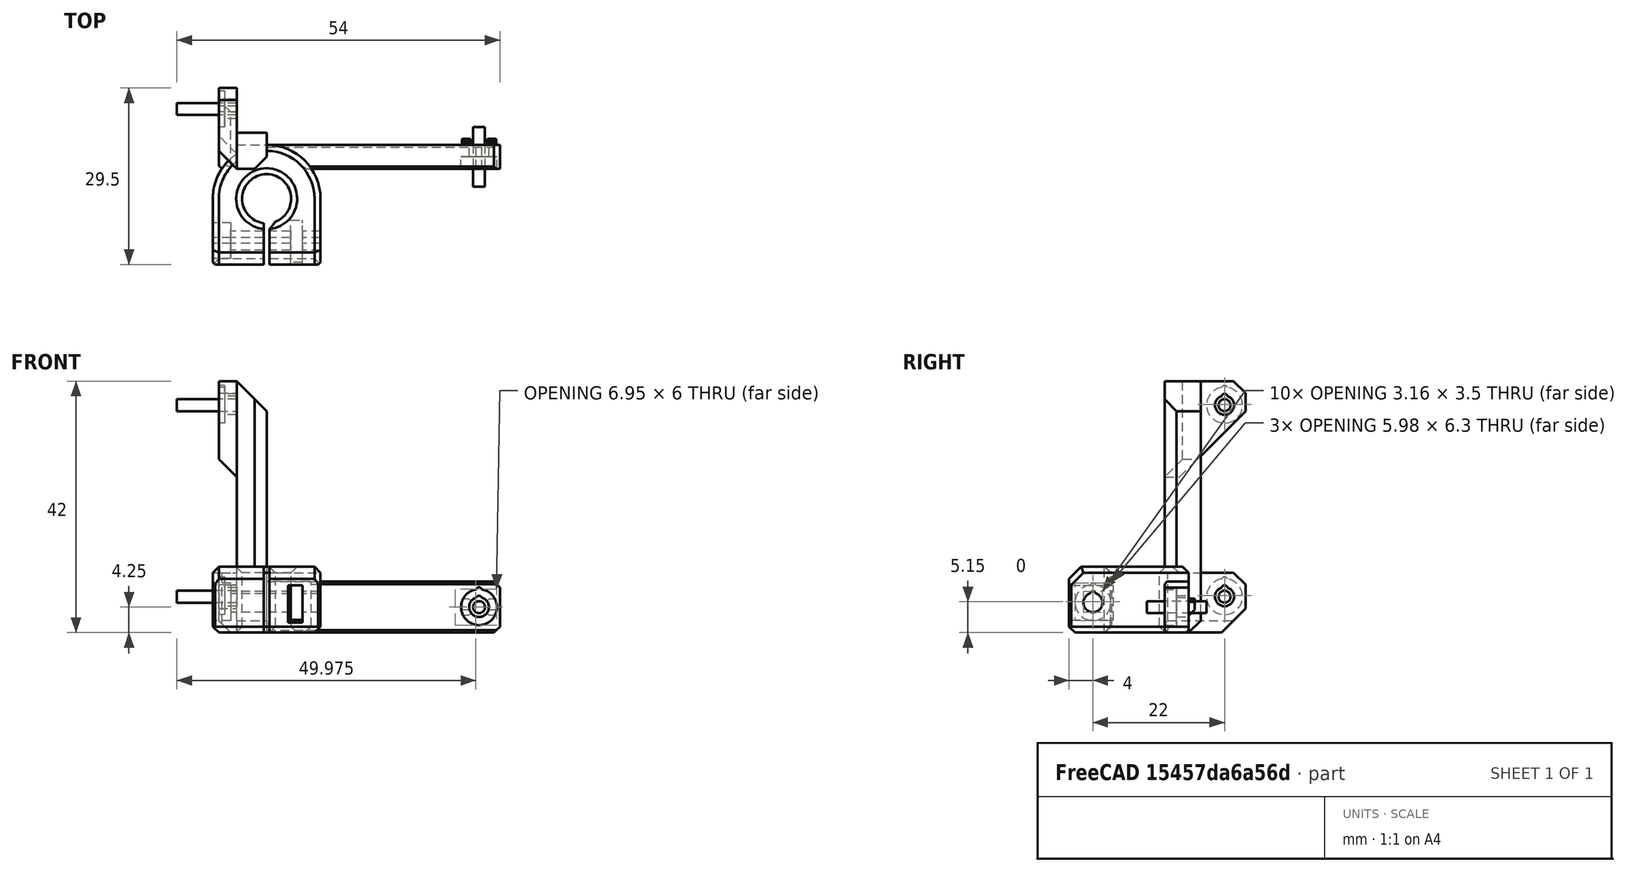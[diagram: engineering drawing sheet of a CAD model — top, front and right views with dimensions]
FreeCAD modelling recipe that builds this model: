
FCSTD DOCUMENT  (FreeCAD 0.18R14555 (Git shallow))
Label: bear-mera-probe-mount
License: All rights reserved
LicenseURL: http://en.wikipedia.org/wiki/All_rights_reserved
objects: Part::Chamfer×19, Part::Cylinder×15, Part::Box×11, Part::Cut×10, Part::MultiFuse×8, Part::Feature×3
note: 66 computed .brp shape members not serialized (recipe doc carries the construction recipe); baked Part::Feature solids carry a one-line shape summary decoded from their .brp

FEATURE [Part::Box] Box001  label="Cube001"
  AttacherType = Attacher::AttachEngine3D
  Height = 8.5
  Length = 44
  Width = 4
FEATURE [Part::Box] Box002  label="Cube002"
  AttacherType = Attacher::AttachEngine3D
  Height = 42
  Length = 5
  Width = 6
FEATURE [Part::Box] Box  label="Cube"
  AttacherType = Attacher::AttachEngine3D
  Height = 10
  Length = 3
  Placement = pos=(-3,0,0) rot=(0,0,1;0rad)
  Width = 13.5
FEATURE [Part::Box] Box003  label="Cube003"
  AttacherType = Attacher::AttachEngine3D
  Height = 16
  Length = 3
  Placement = pos=(-3,0,26) rot=(0,0,1;0rad)
  Width = 13.5
FEATURE [Part::Cylinder] Cylinder
  Angle = 360
  AttacherType = Attacher::AttachEngine3D
  Height = 1
  Placement = pos=(-2,9.5,8.8) rot=(0,-1,0;1.5708rad)
  Radius = 0.5
FEATURE [Part::Cylinder] Cylinder001
  Angle = 360
  AttacherType = Attacher::AttachEngine3D
  Height = 1
  Placement = pos=(-2,9.5,40.8) rot=(0,-1,0;1.5708rad)
  Radius = 0.5
FEATURE [Part::Box] Box004  label="Cube004"
  AttacherType = Attacher::AttachEngine3D
  Height = 10
  Length = 10
  Placement = pos=(-10,0,5) rot=(0,0,1;0rad)
  Width = 10
FEATURE [Part::Chamfer] Chamfer004
  Base = -> Box004
  Edges = 1 edges r=3: [Edge6]
  Placement = pos=(0,0,14) rot=(0,0,1;0rad)
FEATURE [Part::Box] Box005  label="Cube005"
  AttacherType = Attacher::AttachEngine3D
  Height = 10
  Length = 10
  Placement = pos=(-16,0,0) rot=(0,0,1;0rad)
  Width = 15
FEATURE [Part::Chamfer] Chamfer005
  Base = -> Box005
  Edges = 1 edges r=4: [Edge6]
  Placement = pos=(7,0,-8) rot=(0,0,1;0rad)
FEATURE [Part::Box] Box006  label="Cube006"
  AttacherType = Attacher::AttachEngine3D
  Height = 10
  Length = 10
  Placement = pos=(0,-2,38) rot=(0,0,1;0rad)
  Width = 10
FEATURE [Part::Chamfer] Chamfer006
  Base = -> Box006
  Edges = 1 edges r=5: [Edge4]
  Placement = pos=(0,0,-1) rot=(0,0,1;0rad)
FEATURE [Part::Feature] Common001001  label="Common002"
  Placement = pos=(39.7,1,3) rot=(-1,0,0;1.5708rad)
  shape: bbox 6.95 x 4 x 7 mm, 227 faces (baked)
FEATURE [Part::Cylinder] Cylinder002
  Angle = 360
  AttacherType = Attacher::AttachEngine3D
  Height = 10
  Placement = pos=(40.25,1e-15,3) rot=(-1,0,0;1.5708rad)
  Radius = 1.65
FEATURE [Part::Box] Box007  label="Cube007"
  AttacherType = Attacher::AttachEngine3D
  Height = 10
  Length = 10
  Placement = pos=(35,0,6) rot=(0,0,1;0rad)
  Width = 10
FEATURE [Part::Box] Box008  label="Cube008"
  AttacherType = Attacher::AttachEngine3D
  Height = 10
  Length = 10
  Placement = pos=(35,0,-10) rot=(0,0,1;0rad)
  Width = 10
FEATURE [Part::Box] Box009  label="Cube009"
  AttacherType = Attacher::AttachEngine3D
  Height = 10
  Length = 10
  Placement = pos=(35,4,-10) rot=(0,0,1;0rad)
  Width = 10
FEATURE [Part::Chamfer] Chamfer007
  Base = -> Box009
  Edges = 1 edges r=3: [Edge10]
  Placement = pos=(0,0,4.6) rot=(0,0,1;0rad)
FEATURE [Part::Cylinder] Cylinder003
  Angle = 360
  AttacherType = Attacher::AttachEngine3D
  Height = 2
  Placement = pos=(40.25,1e-15,3) rot=(-1,0,0;1.5708rad)
  Radius = 3
FEATURE [Part::Cut] Cut009002
  Base = -> Common001001
  Tool = -> Box008
FEATURE [Part::Cut] Cut009003
  Base = -> Cut009002
  Tool = -> Box007
FEATURE [Part::Cut] Cut009004
  Base = -> Cut009003
  Placement = pos=(0.75,0,1.25) rot=(0,0,1;0rad)
  Tool = -> Chamfer007
FEATURE [Part::Cylinder] Cylinder004
  Angle = 360
  AttacherType = Attacher::AttachEngine3D
  Height = 2
  Placement = pos=(40.25,0,5.8) rot=(-1,0,0;1.5708rad)
  Radius = 0.5
FEATURE [Part::Cylinder] Cylinder005
  Angle = 360
  AttacherType = Attacher::AttachEngine3D
  Height = 4
  Placement = pos=(40.25,1e-15,4.4) rot=(-1,0,0;1.5708rad)
  Radius = 0.5
FEATURE [Part::Box] Box015  label="Cube015"
  AttacherType = Attacher::AttachEngine3D
  Height = 21
  Length = 10
  Placement = pos=(-10,-7,24) rot=(0,0,1;0rad)
  Width = 10
FEATURE [Part::Chamfer] Chamfer017
  Base = -> Box015
  Edges = 1 edges r=3: [Edge7]
FEATURE [Part::Cylinder] Cylinder012
  Angle = 360
  AttacherType = Attacher::AttachEngine3D
  Height = 10
  Placement = pos=(6e-15,9.5,39.4) rot=(0,-1,0;1.5708rad)
  Radius = 0.5
FEATURE [Part::Cylinder] Cylinder013
  Angle = 360
  AttacherType = Attacher::AttachEngine3D
  Height = 10
  Placement = pos=(-1e-15,9.5,7.4) rot=(0,-1,0;1.5708rad)
  Radius = 0.5
FEATURE [Part::Cylinder] Cylinder014
  Angle = 360
  AttacherType = Attacher::AttachEngine3D
  Height = 10
  Placement = pos=(-1e-15,9.5,6) rot=(0,-1,0;1.5708rad)
  Radius = 1.6
FEATURE [Part::Cylinder] Cylinder015
  Angle = 360
  AttacherType = Attacher::AttachEngine3D
  Height = 10
  Placement = pos=(6.1e-15,9.5,38) rot=(0,-1,0;1.5708rad)
  Radius = 1.6
FEATURE [Part::MultiFuse] Fusion003
  Shapes = -> [Cylinder015,Cylinder012]
FEATURE [Part::MultiFuse] Fusion004
  Shapes = -> [Cylinder014,Cylinder013]
FEATURE [Part::Cylinder] Cylinder016
  Angle = 360
  AttacherType = Attacher::AttachEngine3D
  Height = 1
  Placement = pos=(-2,9.5,6) rot=(0,-1,0;1.5708rad)
  Radius = 3
FEATURE [Part::Cylinder] Cylinder017
  Angle = 360
  AttacherType = Attacher::AttachEngine3D
  Height = 1
  Placement = pos=(-2,9.5,38) rot=(0,-1,0;1.5708rad)
  Radius = 3
FEATURE [Part::Chamfer] Chamfer016009
  Base = -> Box002
  Edges = 2 edges r=2: [Edge5,Edge11]
FEATURE [Part::Cut] Cut009023
  Base = -> Chamfer016009
  Tool = -> Chamfer006
FEATURE [Part::Feature] Cut009025001  label="Cut009026"
  shape: bbox 18 x 20 x 11 mm, 41 faces (baked)
FEATURE [Part::Chamfer] Chamfer016012
  Base = -> Cut009025001
  Edges = 2 edges r=2: [Edge12,Edge65]
FEATURE [Part::Chamfer] Chamfer016013
  Base = -> Chamfer016012
  Edges = 2 edges r=1: [Edge2,Edge61]
FEATURE [Part::Chamfer] Chamfer016014
  Base = -> Chamfer016013
  Edges = 2 edges r=1: [Edge14,Edge47]
FEATURE [Part::Chamfer] Chamfer016015
  Base = -> Chamfer016014
  Edges = 2 edges r=0.4: [Edge4,Edge102]
FEATURE [Part::Chamfer] Chamfer016016
  Base = -> Chamfer016015
  Edges = 2 edges r=0.4: [Edge111,Edge112]
FEATURE [Part::MultiFuse] Fusion
  Placement = pos=(0.25,0,1.25) rot=(0,0,1;0rad)
  Shapes = -> [Cylinder005,Cylinder004,Cylinder003,Cylinder002]
FEATURE [Part::MultiFuse] Fusion006
  Placement = pos=(0,0.5,0) rot=(0,0,1;0rad)
  Shapes = -> [Fusion004,Cylinder016,Cylinder]
FEATURE [Part::Cut] Cut009025003
  Base = -> Box
  Tool = -> Fusion006
FEATURE [Part::Chamfer] Chamfer
  Base = -> Cut009025003
  Edges = 1 edges r=4: [Edge13]
FEATURE [Part::Chamfer] Chamfer016019
  Base = -> Chamfer
  Edges = 1 edges r=2: [Edge17]
FEATURE [Part::Cut] Cut009025004
  Base = -> Chamfer016019
  Tool = -> Chamfer005
FEATURE [Part::MultiFuse] Fusion007
  Placement = pos=(0,0.5,0) rot=(0,0,1;0rad)
  Shapes = -> [Fusion003,Cylinder017,Cylinder001]
FEATURE [Part::Cut] Cut
  Base = -> Box003
  Tool = -> Fusion007
FEATURE [Part::Chamfer] Chamfer016020
  Base = -> Cut
  Edges = 1 edges r=11: [Edge13]
FEATURE [Part::Chamfer] Chamfer016021
  Base = -> Chamfer016020
  Edges = 1 edges r=2: [Edge17]
FEATURE [Part::Cut] Cut009025005
  Base = -> Chamfer016021
  Tool = -> Chamfer004
FEATURE [Part::Cut] Cut009025006
  Base = -> Cut009025005
  Tool = -> Chamfer017
FEATURE [Part::MultiFuse] Fusion008
  Shapes = -> [Box001,Cut009004]
FEATURE [Part::Cut] Cut009025007
  Base = -> Fusion008
  Tool = -> Fusion
FEATURE [Part::Chamfer] Chamfer016022
  Base = -> Cut009025007
  Edges = 2 edges r=1: [Edge12,Edge21]
FEATURE [Part::Chamfer] Chamfer016023
  Base = -> Chamfer016022
  Edges = 2 edges r=0.4: [Edge1,Edge5]
FEATURE [Part::Chamfer] Chamfer016024
  Base = -> Chamfer016023
  Edges = 1 edges r=0.4: [Edge32]
FEATURE [Part::Chamfer] Chamfer016025
  Base = -> Cut009025004
  Edges = 1 edges r=0.5: [Edge4]
FEATURE [Part::MultiFuse] Fusion009
  Shapes = -> [Chamfer016025,Chamfer016016,Cut009025006,Cut009023,Chamfer016024]
FEATURE [Part::Feature] Fusion009001  label="Fusion010"
  shape: bbox 48 x 29.5 x 42 mm, 191 faces (baked)
FEATURE [Part::Cylinder] Cylinder018
  Angle = 360
  AttacherType = Attacher::AttachEngine3D
  Height = 10
  Placement = pos=(-1.3e-15,10,6) rot=(0,1,0;4.71239rad)
  Radius = 1
FEATURE [Part::Cylinder] Cylinder019
  Angle = 360
  AttacherType = Attacher::AttachEngine3D
  Height = 10
  Placement = pos=(6.1e-15,10,38) rot=(0,-1,0;1.5708rad)
  Radius = 1
FEATURE [Part::Cylinder] Cylinder020
  Angle = 360
  AttacherType = Attacher::AttachEngine3D
  Height = 10
  Placement = pos=(40.5,7,4.25) rot=(1,0,0;1.5708rad)
  Radius = 1
FEATURE [Part::MultiFuse] Fusion009002  label="screw-pos"
  Shapes = -> [Cylinder020,Cylinder018,Cylinder019]
